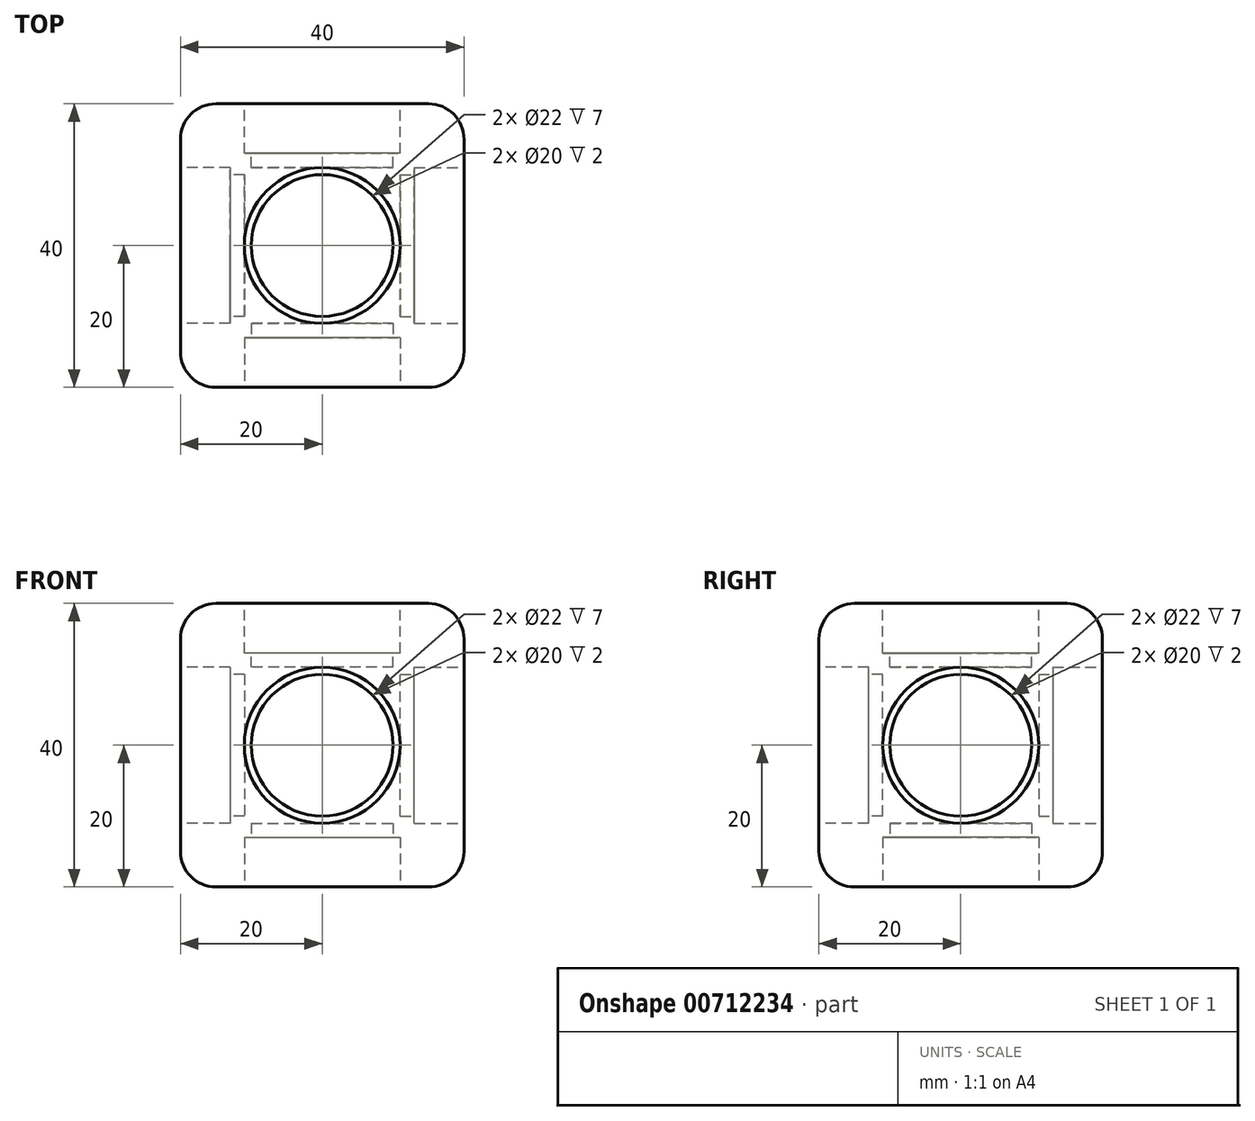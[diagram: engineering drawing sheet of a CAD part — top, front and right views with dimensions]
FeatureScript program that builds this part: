
annotation { "Feature Type Name" : "Feature", "Feature Type Description" : "" }
export const myFeature = defineFeature(function(context is Context, id is Id, definition is map)
    precondition{}
    {
        {
            var Q0;
            Q0=qCreatedBy(makeId("Top.planeOp"),FACE);
            var sketch = newSketch(context, id + "F0", { "sketchPlane" : qUnion([Q0])});
            skLineSegment(sketch, "E0", {"start": v(0, 0) * mm, "end": v(40, 0) * mm});
            skLineSegment(sketch, "E1", {"start": v(40, 0) * mm, "end": v(40, 40) * mm});
            skLineSegment(sketch, "E2", {"start": v(40, 40) * mm, "end": v(0, 40) * mm});
            skLineSegment(sketch, "E3", {"start": v(0, 0) * mm, "end": v(0, 40) * mm});
            skSolve(sketch);
        }
        {
            var Q0;
            Q0=makeQuery(id+"F0.imprint","IMPRINT",FACE,{"disambiguationData":[TD([[makeQuery(id+"F0.imprint","IMPRINT",EDGE,{"derivedFrom":sQuery(id+"F0.wireOp",EDGE,"E0")}),1.0]])]});
            extrude(context, id + "F1", {"entities" : qUnion([Q0]), "depth" : 40 * mm, "offsetDistance" : 25 * mm});
        }
        {
            var Q0;
            Q0=makeQuery(id+"F1.opExtrude","CAP_EDGE",EDGE,{"disambiguationData":[OSD([sQuery(id+"F0.wireOp",EDGE,"E1")])],"isStart":false});
            var Q1;
            Q1=makeQuery(id+"F1.opExtrude","CAP_EDGE",EDGE,{"disambiguationData":[OSD([sQuery(id+"F0.wireOp",EDGE,"E0")])],"isStart":false});
            var Q2;
            Q2=makeQuery(id+"F1.opExtrude","SWEPT_FACE",FACE,{"disambiguationData":[OSD([sQuery(id+"F0.wireOp",EDGE,"E0")])]});
            var Q3;
            Q3=makeQuery(id+"F1.opExtrude","CAP_EDGE",EDGE,{"disambiguationData":[OSD([sQuery(id+"F0.wireOp",EDGE,"E3")])],"isStart":false});
            var Q4;
            Q4=makeQuery(id+"F1.opExtrude","CAP_EDGE",EDGE,{"disambiguationData":[OSD([sQuery(id+"F0.wireOp",EDGE,"E2")])],"isStart":false});
            var Q5;
            Q5=makeQuery(id+"F1.opExtrude","SWEPT_EDGE",EDGE,{"disambiguationData":[OSD([sQuery(id+"F0.wireOp",EDGE,"E1"),sQuery(id+"F0.wireOp",EDGE,"E2")])]});
            var Q6;
            Q6=makeQuery(id+"F1.opExtrude","SWEPT_FACE",FACE,{"disambiguationData":[OSD([sQuery(id+"F0.wireOp",EDGE,"E1")])]});
            var Q7;
            Q7=makeQuery(id+"F1.opExtrude","CAP_EDGE",EDGE,{"disambiguationData":[OSD([sQuery(id+"F0.wireOp",EDGE,"E1")])],"isStart":true});
            var Q8;
            Q8=makeQuery(id+"F1.opExtrude","CAP_EDGE",EDGE,{"disambiguationData":[OSD([sQuery(id+"F0.wireOp",EDGE,"E2")])],"isStart":true});
            var Q9;
            Q9=makeQuery(id+"F1.opExtrude","SWEPT_FACE",FACE,{"disambiguationData":[OSD([sQuery(id+"F0.wireOp",EDGE,"E2")])]});
            var Q10;
            Q10=makeQuery(id+"F1.opExtrude","CAP_EDGE",EDGE,{"disambiguationData":[OSD([sQuery(id+"F0.wireOp",EDGE,"E3")])],"isStart":true});
            var Q11;
            Q11=makeQuery(id+"F1.opExtrude","CAP_FACE",FACE,{"disambiguationData":[OSD([sQuery(id+"F0.wireOp",EDGE,"E0"),sQuery(id+"F0.wireOp",EDGE,"E1"),sQuery(id+"F0.wireOp",EDGE,"E2"),sQuery(id+"F0.wireOp",EDGE,"E3")])],"isStart":true});
            fillet(context, id + "F2", {"entities" : qUnion([Q0, Q1, Q2, Q3, Q4, Q5, Q6, Q7, Q8, Q9, Q10, Q11]), "radius" : 5 * mm, "tangentPropagation" : true, "allowEdgeOverflow" : false});
        }
        {
            var Q0;
            Q0=makeQuery(id+"F1.opExtrude","SWEPT_FACE",FACE,{"disambiguationData":[OSD([sQuery(id+"F0.wireOp",EDGE,"E0")])]});
            var sketch = newSketch(context, id + "F3", { "sketchPlane" : qUnion([Q0])});
            skCircle(sketch, "E4", {"center": v(20, 20) * mm, "radius": 11 * mm});
            skPoint(sketch, "E4.centerSnap0", {"position": v(20, 35) * mm});
            skPoint(sketch, "E4.centerSnap1", {"position": v(5, 20) * mm});
            skSolve(sketch);
        }
        {
            var Q0;
            Q0=makeQuery(id+"F3.imprint","IMPRINT",FACE,{"disambiguationData":[TD([[makeQuery(id+"F3.imprint","IMPRINT",EDGE,{"derivedFrom":sQuery(id+"F3.wireOp",EDGE,"E4")}),1.0]])]});
            extrude(context, id + "F4", {"entities" : qUnion([Q0]), "operationType" : NewBodyOperationType.REMOVE, "oppositeDirection" : true, "depth" : 7 * mm, "offsetDistance" : 25 * mm});
        }
        {
            var Q0;
            Q0=makeQuery(id+"F1.opExtrude","SWEPT_FACE",FACE,{"disambiguationData":[OSD([sQuery(id+"F0.wireOp",EDGE,"E3")])]});
            var sketch = newSketch(context, id + "F5", { "sketchPlane" : qUnion([Q0])});
            skCircle(sketch, "E5", {"center": v(-20, 20) * mm, "radius": 11 * mm});
            skPoint(sketch, "E5.centerSnap0", {"position": v(-35, 20) * mm});
            skPoint(sketch, "E5.centerSnap1", {"position": v(-20, 35) * mm});
            skSolve(sketch);
        }
        {
            var Q0;
            Q0 = qSketchRegion(id + "F5", true);
            extrude(context, id + "F6", {"entities" : qUnion([Q0]), "operationType" : NewBodyOperationType.REMOVE, "oppositeDirection" : true, "depth" : 7 * mm, "offsetDistance" : 25 * mm});
        }
        {
            var Q0;
            Q0=makeQuery(id+"F1.opExtrude","SWEPT_FACE",FACE,{"disambiguationData":[OSD([sQuery(id+"F0.wireOp",EDGE,"E2")])]});
            var sketch = newSketch(context, id + "F7", { "sketchPlane" : qUnion([Q0])});
            skCircle(sketch, "E6", {"center": v(-20, 20) * mm, "radius": 11 * mm});
            skPoint(sketch, "E6.centerSnap0", {"position": v(-35, 20) * mm});
            skPoint(sketch, "E6.centerSnap1", {"position": v(-20, 35) * mm});
            skSolve(sketch);
        }
        {
            var Q0;
            Q0 = qSketchRegion(id + "F7", true);
            extrude(context, id + "F8", {"entities" : qUnion([Q0]), "operationType" : NewBodyOperationType.REMOVE, "oppositeDirection" : true, "depth" : 7 * mm, "offsetDistance" : 25 * mm});
        }
        {
            var Q0;
            Q0=makeQuery(id+"F1.opExtrude","SWEPT_FACE",FACE,{"disambiguationData":[OSD([sQuery(id+"F0.wireOp",EDGE,"E1")])]});
            var sketch = newSketch(context, id + "F9", { "sketchPlane" : qUnion([Q0])});
            skCircle(sketch, "E7", {"center": v(20, 20) * mm, "radius": 11 * mm});
            skPoint(sketch, "E7.centerSnap0", {"position": v(5, 20) * mm});
            skPoint(sketch, "E7.centerSnap1", {"position": v(20, 35) * mm});
            skSolve(sketch);
        }
        {
            var Q0;
            Q0 = qSketchRegion(id + "F9", true);
            extrude(context, id + "F10", {"entities" : qUnion([Q0]), "operationType" : NewBodyOperationType.REMOVE, "oppositeDirection" : true, "depth" : 7 * mm, "offsetDistance" : 25 * mm});
        }
        {
            var Q0;
            Q0=makeQuery(id+"F1.opExtrude","CAP_FACE",FACE,{"disambiguationData":[OSD([sQuery(id+"F0.wireOp",EDGE,"E0"),sQuery(id+"F0.wireOp",EDGE,"E1"),sQuery(id+"F0.wireOp",EDGE,"E2"),sQuery(id+"F0.wireOp",EDGE,"E3")])],"isStart":true});
            var sketch = newSketch(context, id + "F11", { "sketchPlane" : qUnion([Q0])});
            skCircle(sketch, "E8", {"center": v(20, -20) * mm, "radius": 11 * mm});
            skPoint(sketch, "E8.centerSnap0", {"position": v(20, -35) * mm});
            skPoint(sketch, "E8.centerSnap1", {"position": v(5, -20) * mm});
            skSolve(sketch);
        }
        {
            var Q0;
            Q0 = qSketchRegion(id + "F11", true);
            extrude(context, id + "F12", {"entities" : qUnion([Q0]), "operationType" : NewBodyOperationType.REMOVE, "oppositeDirection" : true, "depth" : 7 * mm, "offsetDistance" : 25 * mm});
        }
        {
            var Q0;
            Q0=makeQuery(id+"F1.opExtrude","CAP_FACE",FACE,{"disambiguationData":[OSD([sQuery(id+"F0.wireOp",EDGE,"E0"),sQuery(id+"F0.wireOp",EDGE,"E1"),sQuery(id+"F0.wireOp",EDGE,"E2"),sQuery(id+"F0.wireOp",EDGE,"E3")])],"isStart":false});
            var sketch = newSketch(context, id + "F13", { "sketchPlane" : qUnion([Q0])});
            skCircle(sketch, "E9", {"center": v(20, 20) * mm, "radius": 11 * mm});
            skPoint(sketch, "E9.centerSnap0", {"position": v(20, 35) * mm});
            skPoint(sketch, "E9.centerSnap1", {"position": v(35, 20) * mm});
            skSolve(sketch);
        }
        {
            var Q0;
            Q0 = qSketchRegion(id + "F13", true);
            extrude(context, id + "F14", {"entities" : qUnion([Q0]), "operationType" : NewBodyOperationType.REMOVE, "oppositeDirection" : true, "depth" : 7 * mm, "offsetDistance" : 25 * mm});
        }
        {
            var Q0;
            Q0=makeQuery(id+"F14.boolean.opBoolean","COPY",FACE,{"derivedFrom":makeQuery(id+"F14.opExtrude","CAP_FACE",FACE,{"disambiguationData":[OSD([sQuery(id+"F13.wireOp",EDGE,"E9")])],"isStart":false})});
            var sketch = newSketch(context, id + "F15", { "sketchPlane" : qUnion([Q0])});
            skCircle(sketch, "E10", {"center": v(20, 20) * mm, "radius": 10 * mm});
            skSolve(sketch);
        }
        {
            var Q0;
            Q0=makeQuery(id+"F15.imprint","IMPRINT",FACE,{"disambiguationData":[TD([[makeQuery(id+"F15.imprint","IMPRINT",EDGE,{"derivedFrom":sQuery(id+"F15.wireOp",EDGE,"E10")}),1.0]])]});
            extrude(context, id + "F16", {"entities" : qUnion([Q0]), "operationType" : NewBodyOperationType.REMOVE, "oppositeDirection" : true, "depth" : 2 * mm, "offsetDistance" : 25 * mm});
        }
        {
            var Q0;
            Q0=makeQuery(id+"F4.boolean.opBoolean","COPY",FACE,{"derivedFrom":makeQuery(id+"F4.opExtrude","CAP_FACE",FACE,{"disambiguationData":[OSD([sQuery(id+"F3.wireOp",EDGE,"E4")])],"isStart":false})});
            var sketch = newSketch(context, id + "F17", { "sketchPlane" : qUnion([Q0])});
            skCircle(sketch, "E11", {"center": v(20, 20) * mm, "radius": 10 * mm});
            skSolve(sketch);
        }
        {
            var Q0;
            Q0 = qSketchRegion(id + "F17", true);
            extrude(context, id + "F18", {"entities" : qUnion([Q0]), "operationType" : NewBodyOperationType.REMOVE, "oppositeDirection" : true, "depth" : 2 * mm, "offsetDistance" : 25 * mm});
        }
        {
            var Q0;
            Q0=makeQuery(id+"F12.boolean.opBoolean","COPY",FACE,{"derivedFrom":makeQuery(id+"F12.opExtrude","CAP_FACE",FACE,{"disambiguationData":[OSD([sQuery(id+"F11.wireOp",EDGE,"E8")])],"isStart":false})});
            var sketch = newSketch(context, id + "F19", { "sketchPlane" : qUnion([Q0])});
            skCircle(sketch, "E12", {"center": v(20, -20) * mm, "radius": 10 * mm});
            skSolve(sketch);
        }
        {
            var Q0;
            Q0 = qSketchRegion(id + "F19", true);
            extrude(context, id + "F20", {"entities" : qUnion([Q0]), "operationType" : NewBodyOperationType.REMOVE, "oppositeDirection" : true, "depth" : 2 * mm, "offsetDistance" : 25 * mm});
        }
        {
            var Q0;
            Q0=makeQuery(id+"F8.boolean.opBoolean","COPY",FACE,{"derivedFrom":makeQuery(id+"F8.opExtrude","CAP_FACE",FACE,{"disambiguationData":[OSD([sQuery(id+"F7.wireOp",EDGE,"E6")])],"isStart":false})});
            var sketch = newSketch(context, id + "F21", { "sketchPlane" : qUnion([Q0])});
            skCircle(sketch, "E13", {"center": v(-20, 20) * mm, "radius": 10 * mm});
            skSolve(sketch);
        }
        {
            var Q0;
            Q0 = qSketchRegion(id + "F21", true);
            extrude(context, id + "F22", {"entities" : qUnion([Q0]), "operationType" : NewBodyOperationType.REMOVE, "oppositeDirection" : true, "depth" : 2 * mm, "offsetDistance" : 25 * mm});
        }
        {
            var Q0;
            Q0=makeQuery(id+"F6.boolean.opBoolean","COPY",FACE,{"derivedFrom":makeQuery(id+"F6.opExtrude","CAP_FACE",FACE,{"disambiguationData":[OSD([sQuery(id+"F5.wireOp",EDGE,"E5")])],"isStart":false})});
            var sketch = newSketch(context, id + "F23", { "sketchPlane" : qUnion([Q0])});
            skCircle(sketch, "E14", {"center": v(-20, 20) * mm, "radius": 10 * mm});
            skSolve(sketch);
        }
        {
            var Q0;
            Q0 = qSketchRegion(id + "F23", true);
            extrude(context, id + "F24", {"entities" : qUnion([Q0]), "operationType" : NewBodyOperationType.REMOVE, "oppositeDirection" : true, "depth" : 2 * mm, "offsetDistance" : 25 * mm});
        }
        {
            var Q0;
            Q0=makeQuery(id+"F10.boolean.opBoolean","COPY",FACE,{"derivedFrom":makeQuery(id+"F10.opExtrude","CAP_FACE",FACE,{"disambiguationData":[OSD([sQuery(id+"F9.wireOp",EDGE,"E7")])],"isStart":false})});
            var sketch = newSketch(context, id + "F25", { "sketchPlane" : qUnion([Q0])});
            skCircle(sketch, "E15", {"center": v(20, 20) * mm, "radius": 10 * mm});
            skSolve(sketch);
        }
        {
            var Q0;
            Q0 = qSketchRegion(id + "F25", true);
            extrude(context, id + "F26", {"entities" : qUnion([Q0]), "operationType" : NewBodyOperationType.REMOVE, "oppositeDirection" : true, "depth" : 2 * mm, "offsetDistance" : 25 * mm});
        }
    });
